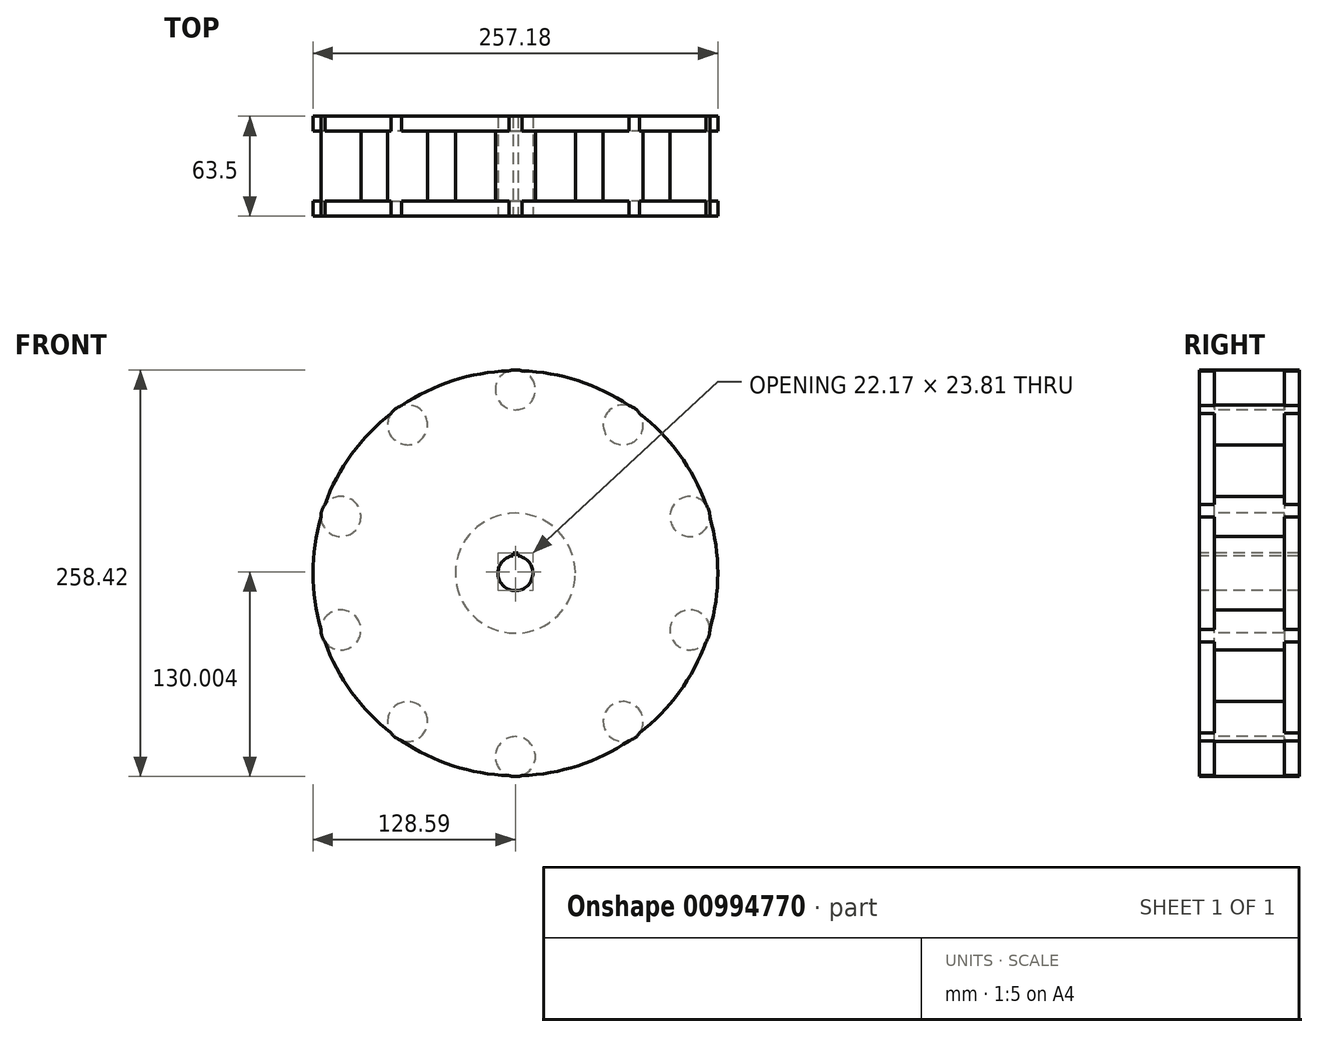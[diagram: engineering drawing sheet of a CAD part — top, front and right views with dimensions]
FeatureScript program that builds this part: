
annotation { "Feature Type Name" : "Feature", "Feature Type Description" : "" }
export const myFeature = defineFeature(function(context is Context, id is Id, definition is map)
    precondition{}
    {
        {
            var Q0;
            Q0=qCreatedBy(makeId("Front.planeOp"),FACE);
            var sketch = newSketch(context, id + "F0", { "sketchPlane" : qUnion([Q0])});
            skCircle(sketch, "E0", {"center": v(0, 0) * mm, "radius": 128.59 * mm});
            skSolve(sketch);
        }
        {
            var Q0;
            Q0 = qSketchRegion(id + "F0", true);
            extrude(context, id + "F1", {"entities" : qUnion([Q0]), "depth" : 63.5 * mm, "offsetDistance" : 25.4 * mm});
        }
        {
            var Q0;
            Q0=qCreatedBy(makeId("Right.planeOp"),FACE);
            var sketch = newSketch(context, id + "F2", { "sketchPlane" : qUnion([Q0])});
            skLineSegment(sketch, "E1", {"start": v(-242.33, 0) * mm, "end": v(0, 0) * mm});
            skLineSegment(sketch, "E2.bottom", {"start": v(-53.98, 139.7) * mm, "end": v(-9.52, 139.7) * mm});
            skLineSegment(sketch, "E2.top", {"start": v(-53.97, 38.1) * mm, "end": v(-9.52, 38.1) * mm});
            skLineSegment(sketch, "E2.left", {"start": v(-53.98, 139.7) * mm, "end": v(-53.97, 38.1) * mm});
            skLineSegment(sketch, "E2.right", {"start": v(-9.53, 139.7) * mm, "end": v(-9.52, 38.1) * mm});
            skSolve(sketch);
        }
        {
            var Q0;
            Q0 = qSketchRegion(id + "F2", true);
            var Q1;
            Q1=sQuery(id+"F2.wireOp",EDGE,"E1");
            revolve(context, id + "F3", {"operationType" : NewBodyOperationType.REMOVE, "surfaceOperationType" : NewSurfaceOperationType.NEW, "entities" : qUnion([Q0]), "axis" : qUnion([Q1]), "revolveType" : RevolveType.SYMMETRIC, "angle" : 360 * degree});
        }
        {
            var Q0;
            Q0=makeQuery(id+"F1.opExtrude","CAP_FACE",FACE,{"disambiguationData":[OSD([sQuery(id+"F0.wireOp",EDGE,"E0")])],"isStart":false});
            var sketch = newSketch(context, id + "F4", { "sketchPlane" : qUnion([Q0])});
            skCircle(sketch, "E3", {"center": v(0, 116.5) * mm, "radius": 12.7 * mm});
            skCircle(sketch, "E4.1.0", {"center": v(-68.48, 94.26) * mm, "radius": 12.7 * mm});
            skCircle(sketch, "E4.2.0", {"center": v(-110.8, 36) * mm, "radius": 12.7 * mm});
            skCircle(sketch, "E4.3.0", {"center": v(-110.8, -36) * mm, "radius": 12.7 * mm});
            skCircle(sketch, "E4.4.0", {"center": v(-68.48, -94.26) * mm, "radius": 12.7 * mm});
            skCircle(sketch, "E4.5.0", {"center": v(0, -116.5) * mm, "radius": 12.7 * mm});
            skCircle(sketch, "E4.6.0", {"center": v(68.48, -94.26) * mm, "radius": 12.7 * mm});
            skCircle(sketch, "E4.7.0", {"center": v(110.8, -36) * mm, "radius": 12.7 * mm});
            skCircle(sketch, "E4.8.0", {"center": v(110.8, 36) * mm, "radius": 12.7 * mm});
            skCircle(sketch, "E4.9.0", {"center": v(68.48, 94.26) * mm, "radius": 12.7 * mm});
            skPoint(sketch, "E4.center", {"position": v(0, 0) * mm});
            skSolve(sketch);
        }
        {
            var Q0;
            Q0 = qSketchRegion(id + "F4", true);
            var Q1;
            Q1=makeQuery(id+"F1.opExtrude","CAP_FACE",FACE,{"disambiguationData":[OSD([sQuery(id+"F0.wireOp",EDGE,"E0")])],"isStart":true});
            extrude(context, id + "F5", {"entities" : qUnion([Q0]), "operationType" : NewBodyOperationType.ADD, "endBound" : BoundingType.UP_TO_SURFACE, "oppositeDirection" : true, "depth" : 25.4 * mm, "endBoundEntityFace" : qUnion([Q1]), "offsetDistance" : 25.4 * mm});
        }
        {
            var Q0;
            Q0=makeQuery(id+"F5.boolean.opBoolean","MERGE",FACE,{"derivedFrom":[makeQuery(id+"F1.opExtrude","CAP_FACE",FACE,{"disambiguationData":[OSD([sQuery(id+"F0.wireOp",EDGE,"E0")])],"isStart":false}),makeQuery(id+"F5.opExtrude","CAP_FACE",FACE,{"disambiguationData":[OSD([sQuery(id+"F4.wireOp",EDGE,"E3")])],"isStart":true}),makeQuery(id+"F5.opExtrude","CAP_FACE",FACE,{"disambiguationData":[OSD([sQuery(id+"F4.wireOp",EDGE,"E4.1.0")])],"isStart":true}),makeQuery(id+"F5.opExtrude","CAP_FACE",FACE,{"disambiguationData":[OSD([sQuery(id+"F4.wireOp",EDGE,"E4.2.0")])],"isStart":true}),makeQuery(id+"F5.opExtrude","CAP_FACE",FACE,{"disambiguationData":[OSD([sQuery(id+"F4.wireOp",EDGE,"E4.3.0")])],"isStart":true}),makeQuery(id+"F5.opExtrude","CAP_FACE",FACE,{"disambiguationData":[OSD([sQuery(id+"F4.wireOp",EDGE,"E4.4.0")])],"isStart":true}),makeQuery(id+"F5.opExtrude","CAP_FACE",FACE,{"disambiguationData":[OSD([sQuery(id+"F4.wireOp",EDGE,"E4.5.0")])],"isStart":true}),makeQuery(id+"F5.opExtrude","CAP_FACE",FACE,{"disambiguationData":[OSD([sQuery(id+"F4.wireOp",EDGE,"E4.6.0")])],"isStart":true}),makeQuery(id+"F5.opExtrude","CAP_FACE",FACE,{"disambiguationData":[OSD([sQuery(id+"F4.wireOp",EDGE,"E4.7.0")])],"isStart":true}),makeQuery(id+"F5.opExtrude","CAP_FACE",FACE,{"disambiguationData":[OSD([sQuery(id+"F4.wireOp",EDGE,"E4.8.0")])],"isStart":true}),makeQuery(id+"F5.opExtrude","CAP_FACE",FACE,{"disambiguationData":[OSD([sQuery(id+"F4.wireOp",EDGE,"E4.9.0")])],"isStart":true})]});
            var sketch = newSketch(context, id + "F6", { "sketchPlane" : qUnion([Q0])});
            skArc(sketch, "E5", {"start": v(-1.59, 11) * mm, "mid": v(0, -11.11) * mm, "end": v(1.59, 11) * mm});
            skLineSegment(sketch, "E6.top", {"start": v(1.59, 12.7) * mm, "end": v(-1.59, 12.7) * mm});
            skLineSegment(sketch, "E6.left", {"start": v(1.59, 11) * mm, "end": v(1.59, 12.7) * mm});
            skLineSegment(sketch, "E6.right", {"start": v(-1.59, 11) * mm, "end": v(-1.59, 12.7) * mm});
            skSolve(sketch);
        }
        {
            var Q0;
            Q0 = qSketchRegion(id + "F6", true);
            extrude(context, id + "F7", {"entities" : qUnion([Q0]), "operationType" : NewBodyOperationType.REMOVE, "endBound" : BoundingType.THROUGH_ALL, "oppositeDirection" : true, "depth" : 25.4 * mm, "offsetDistance" : 25.4 * mm});
        }
    });
